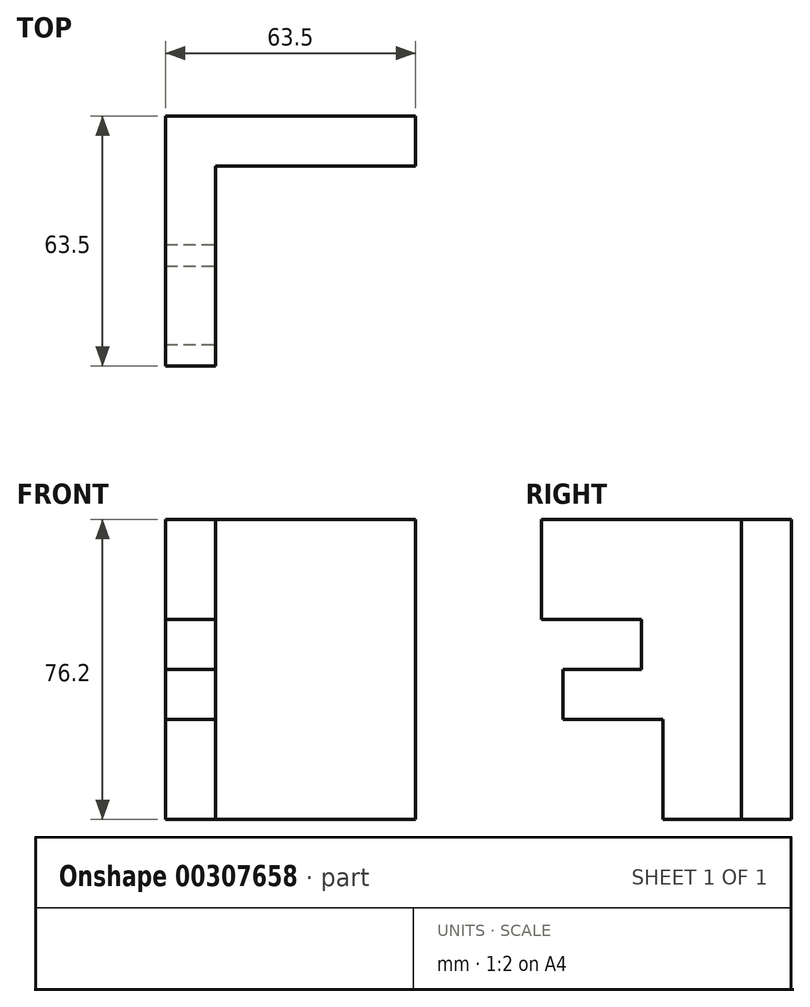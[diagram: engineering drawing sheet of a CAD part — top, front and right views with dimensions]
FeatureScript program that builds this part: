
annotation { "Feature Type Name" : "Feature", "Feature Type Description" : "" }
export const myFeature = defineFeature(function(context is Context, id is Id, definition is map)
    precondition{}
    {
        {
            var Q0;
            Q0=qCreatedBy(makeId("Front.planeOp"),FACE);
            var sketch = newSketch(context, id + "F0", { "sketchPlane" : qUnion([Q0])});
            skLineSegment(sketch, "E0", {"start": v(-32.15, 42.35) * mm, "end": v(31.35, 42.35) * mm});
            skLineSegment(sketch, "E1", {"start": v(31.35, 42.35) * mm, "end": v(31.35, -33.85) * mm});
            skLineSegment(sketch, "E2", {"start": v(31.35, -33.85) * mm, "end": v(-32.15, -33.85) * mm});
            skLineSegment(sketch, "E3", {"start": v(-32.15, -33.85) * mm, "end": v(-32.15, 42.35) * mm});
            skSolve(sketch);
        }
        {
            var Q0;
            Q0 = qSketchRegion(id + "F0", true);
            extrude(context, id + "F1", {"entities" : qUnion([Q0]), "depth" : 12.7 * mm});
        }
        {
            var Q0;
            Q0=makeQuery(id+"F1.opExtrude","CAP_FACE",FACE,{"disambiguationData":[OSD([sQuery(id+"F0.wireOp",EDGE,"E0"),sQuery(id+"F0.wireOp",EDGE,"E1"),sQuery(id+"F0.wireOp",EDGE,"E2"),sQuery(id+"F0.wireOp",EDGE,"E3")])],"isStart":false});
            var sketch = newSketch(context, id + "F2", { "sketchPlane" : qUnion([Q0])});
            skLineSegment(sketch, "E4", {"start": v(-32.15, 42.35) * mm, "end": v(-32.15, -33.85) * mm});
            skLineSegment(sketch, "E5", {"start": v(-32.15, -33.85) * mm, "end": v(-19.45, -33.85) * mm});
            skLineSegment(sketch, "E6", {"start": v(-19.45, -33.85) * mm, "end": v(-19.45, 42.35) * mm});
            skLineSegment(sketch, "E7", {"start": v(-19.45, 42.35) * mm, "end": v(-32.15, 42.35) * mm});
            skSolve(sketch);
        }
        {
            var Q0;
            Q0 = qSketchRegion(id + "F2", true);
            extrude(context, id + "F3", {"entities" : qUnion([Q0]), "operationType" : NewBodyOperationType.ADD, "depth" : 50.8 * mm});
        }
        {
            var Q0;
            Q0=makeQuery(id+"F3.opExtrude","SWEPT_FACE",FACE,{"disambiguationData":[OSD([sQuery(id+"F2.wireOp",EDGE,"E6")])]});
            var sketch = newSketch(context, id + "F4", { "sketchPlane" : qUnion([Q0])});
            skLineSegment(sketch, "E8.bottom", {"start": v(-63.5, 16.95) * mm, "end": v(-38.1, 16.95) * mm});
            skLineSegment(sketch, "E8.top", {"start": v(-63.5, 4.25) * mm, "end": v(-38.1, 4.25) * mm});
            skLineSegment(sketch, "E8.left", {"start": v(-63.5, 16.95) * mm, "end": v(-63.5, 4.25) * mm});
            skLineSegment(sketch, "E8.right", {"start": v(-38.1, 16.95) * mm, "end": v(-38.1, 4.25) * mm});
            skLineSegment(sketch, "E9", {"start": v(-63.5, 16.95) * mm, "end": v(-63.5, 42.35) * mm});
            skLineSegment(sketch, "E10", {"start": v(-58.06, 4.25) * mm, "end": v(-58.06, -21.15) * mm});
            skLineSegment(sketch, "E11", {"start": v(-58.06, -21.15) * mm, "end": v(-63.5, -21.15) * mm});
            skLineSegment(sketch, "E12", {"start": v(-63.5, -21.15) * mm, "end": v(-63.5, 4.25) * mm});
            skLineSegment(sketch, "E13", {"start": v(-63.5, 4.25) * mm, "end": v(-58.06, 4.25) * mm});
            skLineSegment(sketch, "E14", {"start": v(-58.06, -21.15) * mm, "end": v(-58.06, -33.85) * mm});
            skLineSegment(sketch, "E15", {"start": v(-58.06, -33.85) * mm, "end": v(-63.5, -33.85) * mm});
            skLineSegment(sketch, "E16", {"start": v(-63.5, -33.85) * mm, "end": v(-63.5, -21.15) * mm});
            skSolve(sketch);
        }
        {
            var Q0;
            Q0=makeQuery(id+"F4.imprint","IMPRINT",FACE,{"disambiguationData":[TD([[makeQuery(id+"F4.imprint","IMPRINT",EDGE,{"derivedFrom":sQuery(id+"F4.wireOp",EDGE,"E8.bottom")}),-1.0]])]});
            var Q1;
            Q1=makeQuery(id+"F4.imprint","IMPRINT",FACE,{"disambiguationData":[TD([[makeQuery(id+"F4.imprint","IMPRINT",EDGE,{"derivedFrom":sQuery(id+"F4.wireOp",EDGE,"E10")}),-1.0]])]});
            var Q2;
            Q2=makeQuery(id+"F4.imprint","IMPRINT",FACE,{"disambiguationData":[TD([[makeQuery(id+"F4.imprint","IMPRINT",EDGE,{"derivedFrom":sQuery(id+"F4.wireOp",EDGE,"E11")}),1.0]])]});
            extrude(context, id + "F5", {"entities" : qUnion([Q0, Q1, Q2]), "operationType" : NewBodyOperationType.REMOVE, "oppositeDirection" : true, "depth" : 12.7 * mm});
        }
        {
            var Q0;
            Q0=makeQuery(id+"F3.opExtrude","SWEPT_FACE",FACE,{"disambiguationData":[OSD([sQuery(id+"F2.wireOp",EDGE,"E6")])]});
            var sketch = newSketch(context, id + "F6", { "sketchPlane" : qUnion([Q0])});
            skLineSegment(sketch, "E17", {"start": v(-58.06, 4.25) * mm, "end": v(-58.06, -8.45) * mm});
            skLineSegment(sketch, "E18", {"start": v(-58.06, -8.45) * mm, "end": v(-32.66, -8.45) * mm});
            skLineSegment(sketch, "E19", {"start": v(-32.66, -8.45) * mm, "end": v(-32.66, -33.85) * mm});
            skLineSegment(sketch, "E20", {"start": v(-32.66, -33.85) * mm, "end": v(-58.06, -33.85) * mm});
            skLineSegment(sketch, "E21", {"start": v(-58.06, -33.85) * mm, "end": v(-58.06, -8.45) * mm});
            skSolve(sketch);
        }
        {
            var Q0;
            Q0=makeQuery(id+"F6.imprint","IMPRINT",FACE,{"disambiguationData":[TD([[makeQuery(id+"F6.imprint","IMPRINT",EDGE,{"derivedFrom":sQuery(id+"F6.wireOp",EDGE,"E18")}),-1.0]])]});
            extrude(context, id + "F7", {"entities" : qUnion([Q0]), "operationType" : NewBodyOperationType.REMOVE, "oppositeDirection" : true, "depth" : 12.7 * mm});
        }
    });
